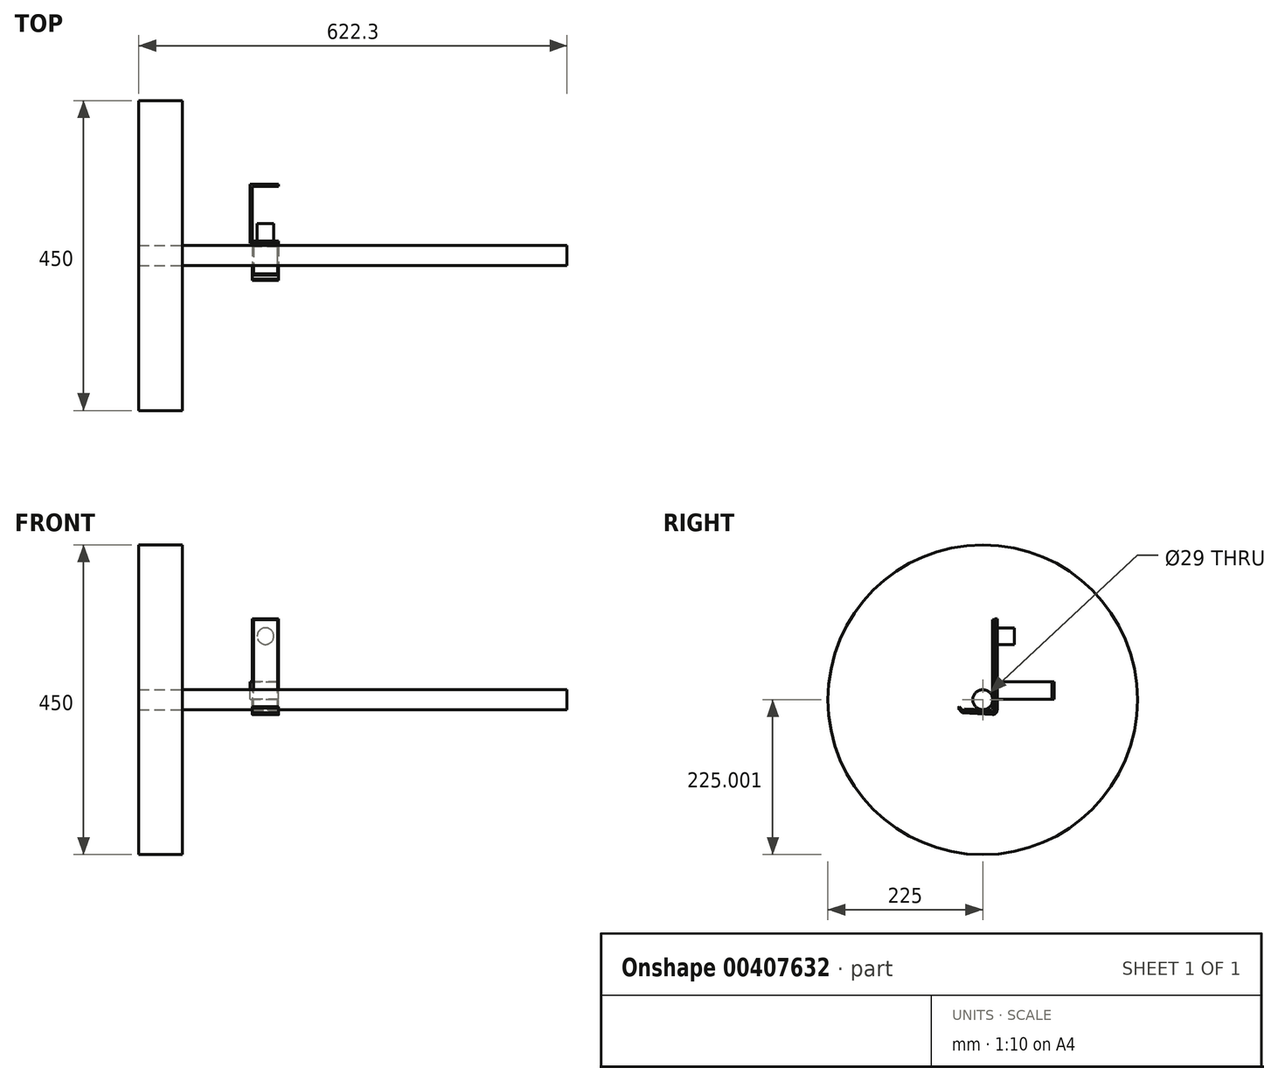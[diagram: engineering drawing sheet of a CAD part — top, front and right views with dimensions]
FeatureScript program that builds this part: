
annotation { "Feature Type Name" : "Feature", "Feature Type Description" : "" }
export const myFeature = defineFeature(function(context is Context, id is Id, definition is map)
    precondition{}
    {
        {
            var Q0;
            Q0=qCreatedBy(makeId("Right.planeOp"),FACE);
            var sketch = newSketch(context, id + "F0", { "sketchPlane" : qUnion([Q0])});
            skLineSegment(sketch, "E0", {"start": v(0, 0) * mm, "end": v(-50.73, 2.66) * mm});
            skLineSegment(sketch, "E1", {"start": v(0, 0) * mm, "end": v(0, 139.7) * mm});
            skLineSegment(sketch, "E2.0", {"start": v(-3.17, 3.35) * mm, "end": v(-49.25, 5.76) * mm});
            skLineSegment(sketch, "E2.1", {"start": v(-3.18, 3.35) * mm, "end": v(-3.18, 139.7) * mm});
            skLineSegment(sketch, "E3", {"start": v(-3.18, 139.7) * mm, "end": v(0, 139.7) * mm});
            skLineSegment(sketch, "E4", {"start": v(-50.73, 2.66) * mm, "end": v(-57.1, 9.74) * mm});
            skLineSegment(sketch, "E5", {"start": v(-57.1, 9.74) * mm, "end": v(-54.74, 11.86) * mm});
            skLineSegment(sketch, "E6", {"start": v(-49.25, 5.76) * mm, "end": v(-54.74, 11.86) * mm});
            skSolve(sketch);
        }
        {
            var Q0;
            Q0 = qSketchRegion(id + "F0", true);
            extrude(context, id + "F1", {"entities" : qUnion([Q0]), "depth" : 38.1 * mm});
        }
        {
            var Q0;
            Q0=makeQuery(id+"F1.opExtrude","SWEPT_EDGE",EDGE,{"disambiguationData":[OSD([sQuery(id+"F0.wireOp",EDGE,"E2.0"),sQuery(id+"F0.wireOp",EDGE,"E2.1")])]});
            fillet(context, id + "F2", {"entities" : qUnion([Q0]), "radius" : 3.17 * mm, "tangentPropagation" : true, "allowEdgeOverflow" : false});
        }
        {
            var Q0;
            Q0=makeQuery(id+"F1.opExtrude","SWEPT_EDGE",EDGE,{"disambiguationData":[OSD([sQuery(id+"F0.wireOp",EDGE,"E0"),sQuery(id+"F0.wireOp",EDGE,"E1")])]});
            fillet(context, id + "F3", {"entities" : qUnion([Q0]), "radius" : 6.35 * mm, "tangentPropagation" : true, "allowEdgeOverflow" : false});
        }
        {
            var Q0;
            Q0=makeQuery(id+"F1.opExtrude","CAP_FACE",FACE,{"disambiguationData":[OSD([sQuery(id+"F0.wireOp",EDGE,"E0"),sQuery(id+"F0.wireOp",EDGE,"E1"),sQuery(id+"F0.wireOp",EDGE,"E2.0"),sQuery(id+"F0.wireOp",EDGE,"E2.1"),sQuery(id+"F0.wireOp",EDGE,"0IwHHgPs-MBZn-dYBJ-IbRS-U48dDVGc21KH"),sQuery(id+"F0.wireOp",EDGE,"E3")])],"isStart":true});
            var sketch = newSketch(context, id + "F4", { "sketchPlane" : qUnion([Q0])});
            skLineSegment(sketch, "E7.bottom", {"start": v(3.17, 22.5) * mm, "end": v(-82.55, 22.5) * mm});
            skLineSegment(sketch, "E7.top", {"start": v(3.17, 47.9) * mm, "end": v(-82.55, 47.9) * mm});
            skLineSegment(sketch, "E7.left", {"start": v(3.18, 22.5) * mm, "end": v(3.18, 47.9) * mm});
            skLineSegment(sketch, "E7.right", {"start": v(-82.55, 22.5) * mm, "end": v(-82.55, 47.9) * mm});
            skSolve(sketch);
        }
        {
            var Q0;
            Q0 = qSketchRegion(id + "F4", true);
            extrude(context, id + "F5", {"entities" : qUnion([Q0]), "operationType" : NewBodyOperationType.ADD, "depth" : 3.17 * mm});
        }
        {
            var Q0;
            Q0=makeQuery(id+"F5.opExtrude","CAP_FACE",FACE,{"disambiguationData":[OSD([sQuery(id+"F4.wireOp",EDGE,"E7.bottom"),sQuery(id+"F4.wireOp",EDGE,"E7.top"),sQuery(id+"F4.wireOp",EDGE,"E7.left"),sQuery(id+"F4.wireOp",EDGE,"E7.right")])],"isStart":true});
            var sketch = newSketch(context, id + "F6", { "sketchPlane" : qUnion([Q0])});
            skLineSegment(sketch, "E8.bottom", {"start": v(82.55, 47.9) * mm, "end": v(79.38, 47.9) * mm});
            skLineSegment(sketch, "E8.top", {"start": v(82.55, 22.5) * mm, "end": v(79.38, 22.5) * mm});
            skLineSegment(sketch, "E8.left", {"start": v(82.55, 47.9) * mm, "end": v(82.55, 22.5) * mm});
            skLineSegment(sketch, "E8.right", {"start": v(79.38, 47.9) * mm, "end": v(79.38, 22.5) * mm});
            skSolve(sketch);
        }
        {
            var Q0;
            Q0 = qSketchRegion(id + "F6", true);
            extrude(context, id + "F7", {"entities" : qUnion([Q0]), "operationType" : NewBodyOperationType.ADD, "depth" : 38.1 * mm});
        }
        {
            var Q0;
            Q0=makeQuery(id+"F1.opExtrude","SWEPT_FACE",FACE,{"disambiguationData":[OSD([sQuery(id+"F0.wireOp",EDGE,"E1")])]});
            var sketch = newSketch(context, id + "F8", { "sketchPlane" : qUnion([Q0])});
            skCircle(sketch, "E9", {"center": v(-19.05, 114.3) * mm, "radius": 12.07 * mm});
            skPoint(sketch, "E9.centerSnap0", {"position": v(-19.05, 139.7) * mm});
            skSolve(sketch);
        }
        {
            var Q0;
            Q0 = qSketchRegion(id + "F8", true);
            extrude(context, id + "F9", {"entities" : qUnion([Q0]), "operationType" : NewBodyOperationType.ADD, "depth" : 25.4 * mm});
        }
        {
            var Q0;
            Q0=makeQuery(id+"F5.boolean.opBoolean","MERGE",FACE,{"derivedFrom":[makeQuery(id+"F1.opExtrude","SWEPT_FACE",FACE,{"disambiguationData":[OSD([sQuery(id+"F0.wireOp",EDGE,"E2.1")])]}),makeQuery(id+"F5.opExtrude","SWEPT_FACE",FACE,{"disambiguationData":[OSD([sQuery(id+"F4.wireOp",EDGE,"E7.left")])]})]});
            var sketch = newSketch(context, id + "F10", { "sketchPlane" : qUnion([Q0])});
            skLineSegment(sketch, "E10.0", {"start": v(1.52, 8.22) * mm, "end": v(36.58, 8.22) * mm});
            skLineSegment(sketch, "E10.1", {"start": v(36.58, 8.22) * mm, "end": v(36.58, 138.18) * mm});
            skLineSegment(sketch, "E10.2", {"start": v(36.58, 138.18) * mm, "end": v(1.52, 138.18) * mm});
            skLineSegment(sketch, "E10.3", {"start": v(1.52, 8.22) * mm, "end": v(1.52, 138.18) * mm});
            skSolve(sketch);
        }
        {
            var Q0;
            Q0 = qSketchRegion(id + "F10", true);
            extrude(context, id + "F11", {"entities" : qUnion([Q0]), "depth" : 3.17 * mm});
        }
        {
            var Q0;
            Q0=makeQuery(id+"F1.opExtrude","SWEPT_FACE",FACE,{"disambiguationData":[OSD([sQuery(id+"F0.wireOp",EDGE,"E2.0")])]});
            var sketch = newSketch(context, id + "F12", { "sketchPlane" : qUnion([Q0])});
            skLineSegment(sketch, "E11.0", {"start": v(36.58, -47.96) * mm, "end": v(36.58, -8.22) * mm});
            skLineSegment(sketch, "E11.1", {"start": v(1.52, -47.96) * mm, "end": v(36.58, -47.96) * mm});
            skLineSegment(sketch, "E11.2", {"start": v(1.52, -8.22) * mm, "end": v(1.52, -47.96) * mm});
            skLineSegment(sketch, "E11.3", {"start": v(36.58, -8.22) * mm, "end": v(1.52, -8.22) * mm});
            skSolve(sketch);
        }
        {
            var Q0;
            Q0 = qSketchRegion(id + "F12", true);
            extrude(context, id + "F13", {"entities" : qUnion([Q0]), "depth" : 3.17 * mm});
        }
        {
            var Q0;
            Q0=qCreatedBy(makeId("Right.planeOp"),FACE);
            var sketch = newSketch(context, id + "F14", { "sketchPlane" : qUnion([Q0])});
            skCircle(sketch, "E12", {"center": v(-20.85, 21.97) * mm, "radius": 14.5 * mm});
            skSolve(sketch);
        }
        {
            var Q0;
            Q0 = qSketchRegion(id + "F14", true);
            extrude(context, id + "F15", {"entities" : qUnion([Q0]), "oppositeDirection" : true, "depth" : 101.6 * mm, "hasSecondDirection" : true, "secondDirectionOppositeDirection" : false, "secondDirectionDepth" : 457.2 * mm});
        }
        {
            var Q0;
            Q0=makeQuery(id+"F15.opExtrude","CAP_FACE",FACE,{"disambiguationData":[OSD([sQuery(id+"F14.wireOp",EDGE,"E12")])],"isStart":false});
            var sketch = newSketch(context, id + "F16", { "sketchPlane" : qUnion([Q0])});
            skCircle(sketch, "E13", {"center": v(20.85, 21.97) * mm, "radius": 225 * mm});
            skSolve(sketch);
        }
        {
            var Q0;
            Q0=makeQuery(id+"F16.imprint","IMPRINT",FACE,{"disambiguationData":[TD([[makeQuery(id+"F16.imprint","IMPRINT",EDGE,{"derivedFrom":sQuery(id+"F16.wireOp",EDGE,"E13")}),1.0]])]});
            extrude(context, id + "F17", {"entities" : qUnion([Q0]), "depth" : 63.5 * mm});
        }
    });
